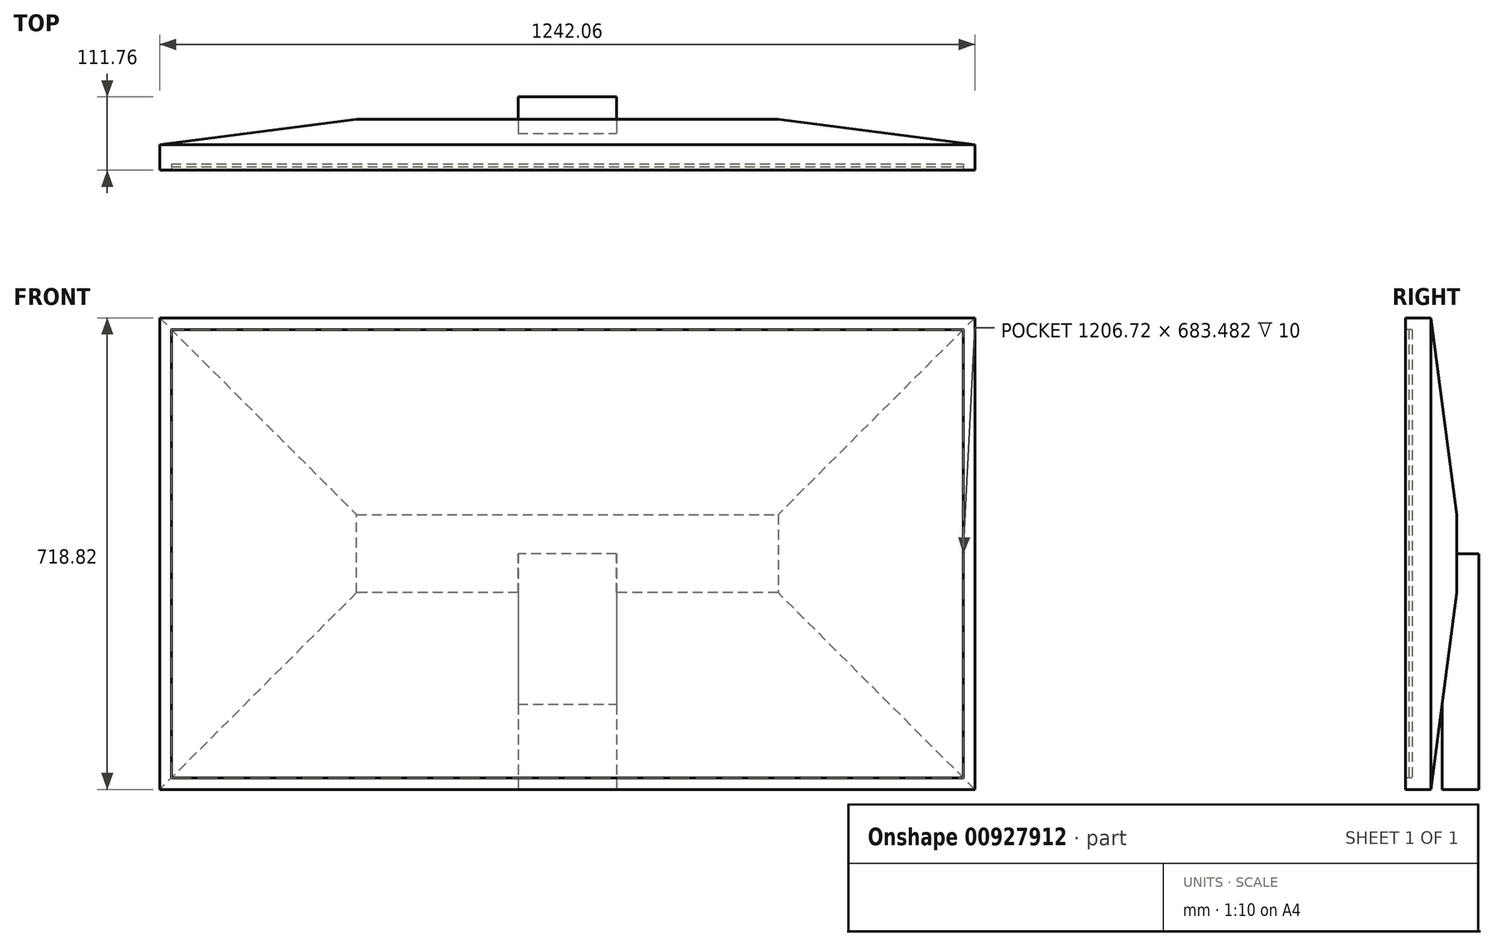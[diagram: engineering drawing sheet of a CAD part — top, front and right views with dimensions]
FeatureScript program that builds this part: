
annotation { "Feature Type Name" : "Feature", "Feature Type Description" : "" }
export const myFeature = defineFeature(function(context is Context, id is Id, definition is map)
    precondition{}
    {
        {
            var Q0;
            Q0=qCreatedBy(makeId("Front.planeOp"),FACE);
            var sketch = newSketch(context, id + "F0", { "sketchPlane" : qUnion([Q0])});
            skLineSegment(sketch, "E0.bottom", {"start": v(-621.03, 779.78) * mm, "end": v(621.03, 779.78) * mm});
            skLineSegment(sketch, "E0.top", {"start": v(-621.03, 60.96) * mm, "end": v(621.03, 60.96) * mm});
            skLineSegment(sketch, "E0.left", {"start": v(-621.03, 779.78) * mm, "end": v(-621.03, 60.96) * mm});
            skLineSegment(sketch, "E0.right", {"start": v(621.03, 779.78) * mm, "end": v(621.03, 60.96) * mm});
            skLineSegment(sketch, "E1", {"start": v(0, 60.96) * mm, "end": v(0, 0) * mm});
            skLineSegment(sketch, "E2.bottom", {"start": v(-603.36, 762.11) * mm, "end": v(603.36, 762.11) * mm});
            skLineSegment(sketch, "E2.top", {"start": v(-603.36, 78.63) * mm, "end": v(603.36, 78.63) * mm});
            skLineSegment(sketch, "E2.left", {"start": v(-603.36, 762.11) * mm, "end": v(-603.36, 78.63) * mm});
            skLineSegment(sketch, "E2.right", {"start": v(603.36, 762.11) * mm, "end": v(603.36, 78.63) * mm});
            skLineSegment(sketch, "E3", {"start": v(0, 762.11) * mm, "end": v(0, 779.78) * mm});
            skLineSegment(sketch, "E4", {"start": v(-603.36, 420.37) * mm, "end": v(-621.03, 420.37) * mm});
            skSolve(sketch);
        }
        {
            var Q0;
            Q0=qCreatedBy(makeId("Right.planeOp"),FACE);
            var sketch = newSketch(context, id + "F1", { "sketchPlane" : qUnion([Q0])});
            skLineSegment(sketch, "E5.bottom", {"start": v(111.76, 779.78) * mm, "end": v(0, 779.78) * mm});
            skLineSegment(sketch, "E5.top", {"start": v(111.76, 60.96) * mm, "end": v(0, 60.96) * mm});
            skLineSegment(sketch, "E5.left", {"start": v(111.76, 779.78) * mm, "end": v(111.76, 60.96) * mm});
            skLineSegment(sketch, "E5.right", {"start": v(0, 779.78) * mm, "end": v(0, 60.96) * mm});
            skLineSegment(sketch, "E6.right", {"start": v(-95, 10) * mm, "end": v(-95, 0) * mm});
            skLineSegment(sketch, "E7", {"start": v(55.88, 420.37) * mm, "end": v(111.76, 420.37) * mm});
            skLineSegment(sketch, "E8", {"start": v(111.76, 420.37) * mm, "end": v(111.76, 10) * mm});
            skLineSegment(sketch, "E9", {"start": v(55.88, 420.37) * mm, "end": v(55.88, 60.96) * mm});
            skLineSegment(sketch, "E10", {"start": v(55.88, 60.96) * mm, "end": v(55.88, 10) * mm});
            skSolve(sketch);
        }
        {
            var Q0;
            {var subQ3=sQuery(id+"F0.wireOp",EDGE,"E3");Q0=makeQuery(id+"F0.imprint","IMPRINT",FACE,{"disambiguationData":[TD([[makeQuery(id+"F0.imprint","IMPRINT",EDGE,{"derivedFrom":subQ3}),1.0]])]});}
            var Q1;
            {var subQ6=sQuery(id+"F0.wireOp",EDGE,"E0.right");Q1=makeQuery(id+"F0.imprint","IMPRINT",FACE,{"disambiguationData":[TD([[makeQuery(id+"F0.imprint","IMPRINT",EDGE,{"derivedFrom":subQ6}),-1.0]])]});}
            var Q2;
            {var subQ4=sQuery(id+"F0.wireOp",EDGE,"E2.top");Q2=makeQuery(id+"F0.imprint","IMPRINT",FACE,{"disambiguationData":[TD([[makeQuery(id+"F0.imprint","IMPRINT",EDGE,{"derivedFrom":subQ4}),1.0]])]});}
            extrude(context, id + "F2", {"entities" : qUnion([Q0, Q1, Q2]), "oppositeDirection" : true, "depth" : 78 * mm, "offsetDistance" : 25 * mm});
        }
        {
            var Q0;
            {var subQ4=sQuery(id+"F0.wireOp",EDGE,"E2.top");Q0=makeQuery(id+"F0.imprint","IMPRINT",FACE,{"disambiguationData":[TD([[makeQuery(id+"F0.imprint","IMPRINT",EDGE,{"derivedFrom":subQ4}),1.0]])]});}
            extrude(context, id + "F3", {"entities" : qUnion([Q0]), "operationType" : NewBodyOperationType.REMOVE, "oppositeDirection" : true, "depth" : 10 * mm, "offsetDistance" : 25 * mm});
        }
        {
            var Q0;
            {var subQ4=sQuery(id+"F0.wireOp",EDGE,"E2.top");Q0=makeQuery(id+"F0.imprint","IMPRINT",FACE,{"disambiguationData":[TD([[makeQuery(id+"F0.imprint","IMPRINT",EDGE,{"derivedFrom":subQ4}),1.0]])]});}
            extrude(context, id + "F4", {"entities" : qUnion([Q0]), "oppositeDirection" : true, "depth" : 10 * mm, "offsetDistance" : 25 * mm, "hasSecondDirection" : true, "secondDirectionOppositeDirection" : true, "secondDirectionDepth" : 5 * mm});
        }
        {
            var Q0;
            Q0=makeQuery(id+"F2.opExtrude","CAP_EDGE",EDGE,{"disambiguationData":[OSD([sQuery(id+"F0.wireOp",EDGE,"E0.bottom")])],"isStart":false});
            var Q1;
            Q1=makeQuery(id+"F2.opExtrude","CAP_EDGE",EDGE,{"disambiguationData":[OSD([sQuery(id+"F0.wireOp",EDGE,"E0.left")])],"isStart":false});
            var Q2;
            Q2=makeQuery(id+"F2.opExtrude","CAP_EDGE",EDGE,{"disambiguationData":[OSD([sQuery(id+"F0.wireOp",EDGE,"E0.top")])],"isStart":false});
            var Q3;
            Q3=makeQuery(id+"F2.opExtrude","CAP_EDGE",EDGE,{"disambiguationData":[OSD([sQuery(id+"F0.wireOp",EDGE,"E0.right")])],"isStart":false});
            chamfer(context, id + "F5", {"entities" : qUnion([Q0, Q1, Q2, Q3]), "chamferType" : ChamferType.TWO_OFFSETS, "width1" : 300 * mm, "oppositeDirection" : false, "width2" : 39 * mm, "tangentPropagation" : true});
        }
        {
            var Q0;
            {var subQ4=sQuery(id+"F1.wireOp",EDGE,"E7");Q0=makeQuery(id+"F1.imprint","IMPRINT",FACE,{"disambiguationData":[TD([[makeQuery(id+"F1.imprint","IMPRINT",EDGE,{"derivedFrom":subQ4}),-1.0]])]});}
            var Q1;
            {var subQ3=sQuery(id+"F1.wireOp",EDGE,"E10");Q1=makeQuery(id+"F1.imprint","IMPRINT",FACE,{"disambiguationData":[TD([[makeQuery(id+"F1.imprint","IMPRINT",EDGE,{"derivedFrom":subQ3}),1.0]])]});}
            extrude(context, id + "F6", {"entities" : qUnion([Q0, Q1]), "operationType" : NewBodyOperationType.ADD, "depth" : 75 * mm, "offsetDistance" : 25 * mm, "hasSecondDirection" : true, "secondDirectionOppositeDirection" : true, "secondDirectionDepth" : 75 * mm});
        }
    });
